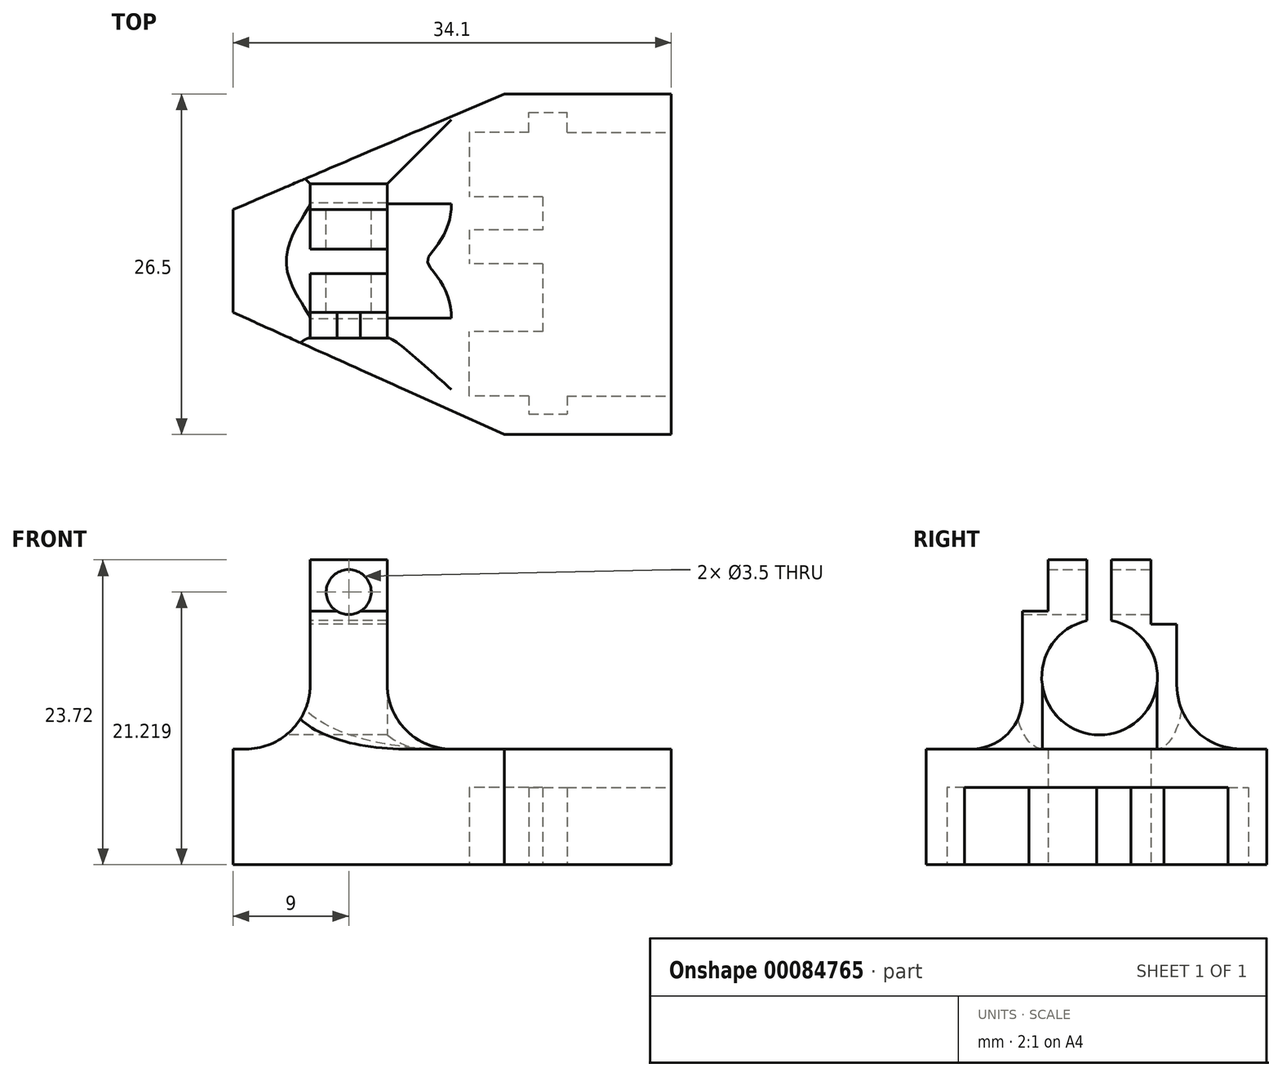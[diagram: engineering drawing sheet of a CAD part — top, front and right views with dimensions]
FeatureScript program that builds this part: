
annotation { "Feature Type Name" : "Feature", "Feature Type Description" : "" }
export const myFeature = defineFeature(function(context is Context, id is Id, definition is map)
    precondition{}
    {
        {
            var Q0;
            Q0=qCreatedBy(makeId("Top.planeOp"),FACE);
            var sketch = newSketch(context, id + "F0", { "sketchPlane" : qUnion([Q0])});
            skLineSegment(sketch, "E0.bottom", {"start": v(20, 10) * mm, "end": v(28.1, 10) * mm});
            skLineSegment(sketch, "E0.top", {"start": v(20, -10.5) * mm, "end": v(28.1, -10.5) * mm});
            skLineSegment(sketch, "E0.left", {"start": v(18.1, 5) * mm, "end": v(18.1, 2.43) * mm});
            skLineSegment(sketch, "E1", {"start": v(28.1, -13.5) * mm, "end": v(15.1, -13.5) * mm});
            skLineSegment(sketch, "E2", {"start": v(15.1, -13.5) * mm, "end": v(-6, -4) * mm});
            skLineSegment(sketch, "E3", {"start": v(-6, -4) * mm, "end": v(-6, 4) * mm});
            skLineSegment(sketch, "E4", {"start": v(-6, 4) * mm, "end": v(15.1, 13) * mm});
            skLineSegment(sketch, "E5", {"start": v(15.1, 13) * mm, "end": v(28.1, 13) * mm});
            skLineSegment(sketch, "E6", {"start": v(28.1, 13) * mm, "end": v(28.1, 10) * mm});
            skLineSegment(sketch, "E7", {"start": v(28.1, -10.5) * mm, "end": v(28.1, -13.5) * mm});
            skLineSegment(sketch, "E8.bottom", {"start": v(17.03, 10) * mm, "end": v(12.39, 10) * mm});
            skLineSegment(sketch, "E8.top", {"start": v(18.1, 5) * mm, "end": v(12.39, 5) * mm});
            skLineSegment(sketch, "E8.right", {"start": v(12.39, 10) * mm, "end": v(12.39, 5) * mm});
            skLineSegment(sketch, "E9.bottom", {"start": v(17.03, -10.5) * mm, "end": v(12.39, -10.5) * mm});
            skLineSegment(sketch, "E9.top", {"start": v(18.1, -5.5) * mm, "end": v(12.39, -5.5) * mm});
            skLineSegment(sketch, "E9.right", {"start": v(12.39, -10.5) * mm, "end": v(12.39, -5.5) * mm});
            skLineSegment(sketch, "E10.bottom", {"start": v(18.1, 2.43) * mm, "end": v(12.39, 2.43) * mm});
            skLineSegment(sketch, "E10.top", {"start": v(18.1, -0.22) * mm, "end": v(12.39, -0.22) * mm});
            skLineSegment(sketch, "E10.right", {"start": v(12.39, 2.43) * mm, "end": v(12.39, -0.22) * mm});
            skLineSegment(sketch, "E11.trimOffspring", {"start": v(18.1, -0.22) * mm, "end": v(18.1, -5.5) * mm});
            skLineSegment(sketch, "E12.top", {"start": v(17.03, 11.57) * mm, "end": v(20, 11.57) * mm});
            skLineSegment(sketch, "E12.left", {"start": v(17.03, 10) * mm, "end": v(17.03, 11.57) * mm});
            skLineSegment(sketch, "E12.right", {"start": v(20, 10) * mm, "end": v(20, 11.57) * mm});
            skLineSegment(sketch, "E13.top", {"start": v(17.03, -11.9) * mm, "end": v(20, -11.9) * mm});
            skLineSegment(sketch, "E13.left", {"start": v(17.03, -10.5) * mm, "end": v(17.03, -11.9) * mm});
            skLineSegment(sketch, "E13.right", {"start": v(20, -10.5) * mm, "end": v(20, -11.9) * mm});
            skSolve(sketch);
        }
        {
            var Q0;
            Q0=qSketchRegion(id+"F0",true);
            extrude(context, id + "F1", {"entities" : qUnion([Q0]), "depth" : 6 * mm});
        }
        {
            var Q0;
            Q0=makeQuery(id+"F1.opExtrude","CAP_FACE",FACE,{"disambiguationData":[OSD([sQuery(id+"F0.wireOp",EDGE,"ZNU6Iqej-mTzt-GtDV-wLe1-LAvuyUocB7eN"),sQuery(id+"F0.wireOp",EDGE,"E0.bottom"),sQuery(id+"F0.wireOp",EDGE,"E0.top"),sQuery(id+"F0.wireOp",EDGE,"E0.left"),sQuery(id+"F0.wireOp",EDGE,"E1"),sQuery(id+"F0.wireOp",EDGE,"E2"),sQuery(id+"F0.wireOp",EDGE,"E3"),sQuery(id+"F0.wireOp",EDGE,"E4"),sQuery(id+"F0.wireOp",EDGE,"E5"),sQuery(id+"F0.wireOp",EDGE,"E6"),sQuery(id+"F0.wireOp",EDGE,"E7"),sQuery(id+"F0.wireOp",EDGE,"E8.bottom"),sQuery(id+"F0.wireOp",EDGE,"E8.top"),sQuery(id+"F0.wireOp",EDGE,"E8.right"),sQuery(id+"F0.wireOp",EDGE,"E9.bottom"),sQuery(id+"F0.wireOp",EDGE,"E9.top"),sQuery(id+"F0.wireOp",EDGE,"E9.right"),sQuery(id+"F0.wireOp",EDGE,"E10.bottom"),sQuery(id+"F0.wireOp",EDGE,"E10.top"),sQuery(id+"F0.wireOp",EDGE,"E10.right"),sQuery(id+"F0.wireOp",EDGE,"E11.trimOffspring")])],"isStart":false});
            var sketch = newSketch(context, id + "F2", { "sketchPlane" : qUnion([Q0])});
            skLineSegment(sketch, "E14", {"start": v(-6, 4) * mm, "end": v(15.1, 13) * mm});
            skLineSegment(sketch, "E15", {"start": v(15.1, 13) * mm, "end": v(28.1, 13) * mm});
            skLineSegment(sketch, "E16", {"start": v(28.1, 13) * mm, "end": v(28.1, -13.5) * mm});
            skLineSegment(sketch, "E17", {"start": v(28.1, -13.5) * mm, "end": v(15.1, -13.5) * mm});
            skLineSegment(sketch, "E18", {"start": v(15.1, -13.5) * mm, "end": v(-6, -4) * mm});
            skLineSegment(sketch, "E19", {"start": v(-6, -4) * mm, "end": v(-6, 4) * mm});
            skSolve(sketch);
        }
        {
            var Q0;
            Q0=qSketchRegion(id+"F2",true);
            extrude(context, id + "F3", {"entities" : qUnion([Q0]), "operationType" : NewBodyOperationType.ADD, "depth" : 3 * mm});
        }
        {
            var Q0;
            Q0=qCreatedBy(makeId("Right.planeOp"),FACE);
            var sketch = newSketch(context, id + "F4", { "sketchPlane" : qUnion([Q0])});
            skArc(sketch, "E20", {"start": v(-0.98, 19) * mm, "mid": v(0.03, 10.1) * mm, "end": v(0.92, 19) * mm});
            skLineSegment(sketch, "E21.bottom", {"start": v(6, 18.72) * mm, "end": v(4, 18.72) * mm});
            skLineSegment(sketch, "E21.top", {"start": v(6, 8.6) * mm, "end": v(-6, 8.6) * mm});
            skLineSegment(sketch, "E21.left", {"start": v(6, 18.72) * mm, "end": v(6, 8.6) * mm});
            skLineSegment(sketch, "E21.right", {"start": v(-6, 19.72) * mm, "end": v(-6, 8.6) * mm});
            skLineSegment(sketch, "E22.top", {"start": v(4, 23.72) * mm, "end": v(0.92, 23.72) * mm});
            skLineSegment(sketch, "E22.left", {"start": v(4, 18.72) * mm, "end": v(4, 23.72) * mm});
            skLineSegment(sketch, "E22.right", {"start": v(-4, 19.72) * mm, "end": v(-4, 23.72) * mm});
            skLineSegment(sketch, "E23.left", {"start": v(0.92, 23.72) * mm, "end": v(0.92, 19) * mm});
            skLineSegment(sketch, "E23.right", {"start": v(-0.98, 23.72) * mm, "end": v(-0.98, 19) * mm});
            skLineSegment(sketch, "E24.trimOffspring", {"start": v(-4, 19.72) * mm, "end": v(-6, 19.72) * mm});
            skLineSegment(sketch, "E25.trimOffspring", {"start": v(-0.98, 23.72) * mm, "end": v(-4, 23.72) * mm});
            skSolve(sketch);
        }
        {
            var Q0;
            Q0 = qSketchRegion(id + "F4", true);
            extrude(context, id + "F5", {"entities" : qUnion([Q0]), "operationType" : NewBodyOperationType.ADD, "depth" : 6 * mm});
        }
        {
            var Q0;
            Q0=makeQuery(id+"F5.opExtrude","SWEPT_FACE",FACE,{"disambiguationData":[OSD([sQuery(id+"F4.wireOp",EDGE,"E22.left")])]});
            var sketch = newSketch(context, id + "F6", { "sketchPlane" : qUnion([Q0])});
            skCircle(sketch, "E26", {"center": v(-3, 21.22) * mm, "radius": 1.75 * mm});
            skSolve(sketch);
        }
        {
            var Q0;
            Q0 = qSketchRegion(id + "F6", true);
            extrude(context, id + "F7", {"entities" : qUnion([Q0]), "operationType" : NewBodyOperationType.REMOVE, "oppositeDirection" : true, "depth" : 25 * mm});
        }
        {
            var Q0;
            Q0=makeQuery(id+"F5.boolean.opBoolean","INTERSECT",EDGE,{"derivedFrom":[makeQuery(id+"F3.opExtrude","CAP_FACE",FACE,{"disambiguationData":[OSD([sQuery(id+"F2.wireOp",EDGE,"E14"),sQuery(id+"F2.wireOp",EDGE,"E15"),sQuery(id+"F2.wireOp",EDGE,"E16"),sQuery(id+"F2.wireOp",EDGE,"E17"),sQuery(id+"F2.wireOp",EDGE,"E18"),sQuery(id+"F2.wireOp",EDGE,"E19")])],"isStart":false}),makeQuery(id+"F5.opExtrude","CAP_FACE",FACE,{"disambiguationData":[OSD([sQuery(id+"F4.wireOp",EDGE,"E20"),sQuery(id+"F4.wireOp",EDGE,"E21.bottom"),sQuery(id+"F4.wireOp",EDGE,"E21.top"),sQuery(id+"F4.wireOp",EDGE,"E21.left"),sQuery(id+"F4.wireOp",EDGE,"E21.right"),sQuery(id+"F4.wireOp",EDGE,"E22.top"),sQuery(id+"F4.wireOp",EDGE,"E22.left"),sQuery(id+"F4.wireOp",EDGE,"E22.right"),sQuery(id+"F4.wireOp",EDGE,"E23.left"),sQuery(id+"F4.wireOp",EDGE,"E23.right"),sQuery(id+"F4.wireOp",EDGE,"E24.trimOffspring"),sQuery(id+"F4.wireOp",EDGE,"E25.trimOffspring")])],"isStart":false})]});
            fillet(context, id + "F8", {"entities" : qUnion([Q0]), "radius" : 5 * mm, "tangentPropagation" : true, "allowEdgeOverflow" : false});
        }
        {
            var Q0;
            Q0=makeQuery(id+"F5.boolean.opBoolean","INTERSECT",EDGE,{"derivedFrom":[makeQuery(id+"F3.opExtrude","CAP_FACE",FACE,{"disambiguationData":[OSD([sQuery(id+"F2.wireOp",EDGE,"E14"),sQuery(id+"F2.wireOp",EDGE,"E15"),sQuery(id+"F2.wireOp",EDGE,"E16"),sQuery(id+"F2.wireOp",EDGE,"E17"),sQuery(id+"F2.wireOp",EDGE,"E18"),sQuery(id+"F2.wireOp",EDGE,"E19")])],"isStart":false}),makeQuery(id+"F5.opExtrude","SWEPT_FACE",FACE,{"disambiguationData":[OSD([sQuery(id+"F4.wireOp",EDGE,"E21.left")])]})]});
            fillet(context, id + "F9", {"entities" : qUnion([Q0]), "radius" : 5 * mm, "tangentPropagation" : true, "allowEdgeOverflow" : false});
        }
        {
            var Q0;
            Q0=makeQuery(id+"F5.boolean.opBoolean","INTERSECT",EDGE,{"derivedFrom":[makeQuery(id+"F3.opExtrude","CAP_FACE",FACE,{"disambiguationData":[OSD([sQuery(id+"F2.wireOp",EDGE,"E14"),sQuery(id+"F2.wireOp",EDGE,"E15"),sQuery(id+"F2.wireOp",EDGE,"E16"),sQuery(id+"F2.wireOp",EDGE,"E17"),sQuery(id+"F2.wireOp",EDGE,"E18"),sQuery(id+"F2.wireOp",EDGE,"E19")])],"isStart":false}),makeQuery(id+"F5.opExtrude","CAP_FACE",FACE,{"disambiguationData":[OSD([sQuery(id+"F4.wireOp",EDGE,"E20"),sQuery(id+"F4.wireOp",EDGE,"E21.bottom"),sQuery(id+"F4.wireOp",EDGE,"E21.top"),sQuery(id+"F4.wireOp",EDGE,"E21.left"),sQuery(id+"F4.wireOp",EDGE,"E21.right"),sQuery(id+"F4.wireOp",EDGE,"E22.top"),sQuery(id+"F4.wireOp",EDGE,"E22.left"),sQuery(id+"F4.wireOp",EDGE,"E22.right"),sQuery(id+"F4.wireOp",EDGE,"E23.left"),sQuery(id+"F4.wireOp",EDGE,"E23.right"),sQuery(id+"F4.wireOp",EDGE,"E24.trimOffspring"),sQuery(id+"F4.wireOp",EDGE,"E25.trimOffspring")])],"isStart":true})]});
            fillet(context, id + "F10", {"entities" : qUnion([Q0]), "radius" : 5 * mm, "tangentPropagation" : true, "allowEdgeOverflow" : false});
        }
        {
            var Q0;
            Q0=makeQuery(id+"F5.boolean.opBoolean","INTERSECT",EDGE,{"derivedFrom":[makeQuery(id+"F3.opExtrude","CAP_FACE",FACE,{"disambiguationData":[OSD([sQuery(id+"F2.wireOp",EDGE,"E14"),sQuery(id+"F2.wireOp",EDGE,"E15"),sQuery(id+"F2.wireOp",EDGE,"E16"),sQuery(id+"F2.wireOp",EDGE,"E17"),sQuery(id+"F2.wireOp",EDGE,"E18"),sQuery(id+"F2.wireOp",EDGE,"E19")])],"isStart":false}),makeQuery(id+"F5.opExtrude","SWEPT_FACE",FACE,{"disambiguationData":[OSD([sQuery(id+"F4.wireOp",EDGE,"E21.right")])]})]});
            fillet(context, id + "F11", {"entities" : qUnion([Q0]), "radius" : 4 * mm, "tangentPropagation" : true, "allowEdgeOverflow" : false});
        }
    });
